# Revit family: Clevertronics_LLIFE-PRO-SM-xx
name_source: partatom
category: Lighting Fixtures
units: mm (PartAtom-declared; Revit-internal decimal feet)

## family parameters
Cut with Voids When Loaded = No
Host = Face
Light Source = Yes
Part Type = Normal
Room Calculation Point = No
Round Connector Dimension = Use Diameter
Shared = No

## types (12) — shared parameters
Apparent Load = 3 VA
Clevertronics_240V LED Strip = 8003081
Clevertronics_AS2293 Classification = C0=D80 C90=D80
Clevertronics_Applicable Standards = AS/NZS3820, CISPR15, AS/NZS2293.3
Clevertronics_Battery = 3.3V 5000mAh
Clevertronics_Battery Type = Lithium Nanophosphate
Clevertronics_Charger Method = Intelligent Current Limited Constant Voltage
Clevertronics_Construction = Polycarbonate Enclosure
Clevertronics_Dimensions Main Enclosure = 242mm x 125mm x 48mm
Clevertronics_Height = 48 mm  [stored 0.15748 ft]
Clevertronics_IP Rating = IP20
Clevertronics_Length = 242 mm  [stored 0.793963 ft]
Clevertronics_Material = Clevertronics_Plycarbonate Base
Clevertronics_Mounting = Surface Mounted
Clevertronics_Operating Mode = Non-maintained
Clevertronics_Operating Temperature = 1˚C to 40˚C
Clevertronics_Operating Voltage = 240V AC; 50Hz
Clevertronics_Replacement Battery = 1530231
Clevertronics_Weight = 0.7Kg
Clevertronics_Width = 125 mm  [stored 0.410105 ft]
Color Filter = 16777215
Default Elevation = 1200 mm
Dimming Lamp Color Temperature Shift = <None>
Lamp = Dual LED (Lifetime warranty on the lamp head and loom assembly)
Manufacturer = Clevertronics
Photometric Web File = LLIFE-PRO-SM_IESA_E_ LL22440_20200331.ies
Tilt Angle = -90.00°
zero-valued in all types: Clevertronics_Annotation Size

## per-type parameters (varying)
| type | Clevertronics_Emergency Driver | Clevertronics_MIC Number | Clevertronics_Power Consumption | Clevertronics_Product Description | Clevertronics_Testing Node | Clevertronics_Testing System | Description | Model |
| LLIFE-PRO-SM_AUT01310080001 | 8003501 | AUT01310080001 | 0.4 Watts (Standby), 2.7 Watts (Max) | Lifelight Pro Emergency, Surface Mount, L10 Nanophosphate, Clevertest Plus |  | Clevertest Plus Enabled (Not activated by default) | Lifelight Pro Emergency, Surface Mount, L10 Nanophosphate, Clevertest Plus | LLIFE-PRO-SM |
| LLIFE-PRO-SM-DALI-BLK_AUT01210580002 | 8003501
8003051 | AUT01210580002 | 0.7 Watts (Standby), 3.0 Watts (Max) | Lifelight Pro Emergency, Surface Mount, L10 Nanophosphate, DALI Emergency, Black | 8003060 | DALI Registered | Lifelight Pro Emergency, Surface Mount, L10 Nanophosphate, DALI Emergency, Black | LLIFE-PRO-SM-DALI-BLK |
| LLIFE-PRO-SM-HV-BLK_AUT02810070001 | 8003501 | AUT02810070001 | 0.7 Watts (Standby), 3.0 Watts (Max) | Lifelight Pro Emergency, Surface Mount, L10 Nanophosphate, Zoneworks XT Hive, Black | 8003191 | Zoneworks XT HIVE (RF) | Lifelight Pro Emergency, Surface Mount, L10 Nanophosphate, Zoneworks XT Hive, Black | LLIFE-PRO-SM-HV-BLK |
| LLIFE-PRO-SM-HV_AUT01810030001 | 8003501
8003501
8003501 | AUT01810030001 | 0.7 Watts (Standby), 3.0 Watts (Max) | Lifelight Pro Emergency, Surface Mount, L10 Nanophosphate, Zoneworks XT Hive | 8003191 | Zoneworks XT HIVE (RF) | Lifelight Pro Emergency, Surface Mount, L10 Nanophosphate, Zoneworks XT Hive | LLIFE-PRO-SM-HV |
| LLIFE-PRO-SM-BLK_AUT01310110001 | 8003501 | AUT01310110001 | 0.4 Watts (Standby), 2.7 Watts (Max) | Lifelight Pro Emergency, Surface Mount, L10 Nanophosphate, Clevertest Plus, Black |  | Clevertest Plus Enabled (Not activated by default) | Lifelight Pro Emergency, Surface Mount, L10 Nanophosphate, Clevertest Plus, Black | LLIFE-PRO-SM-BLK |
| LLIFE-PRO-SM-ZW_AUT01110070001 | 8003501 | AUT01110070001 | 0.7 Watts (Standby), 3.0 Watts (Max) | Lifelight Pro Emergency, Surface Mount, L10 Nanophosphate, Zoneworks | 8001450 | Zoneworks Computerised Testing | Lifelight Pro Emergency, Surface Mount, L10 Nanophosphate, Zoneworks | LLIFE-PRO-SM-ZW |
| LLIFE-PRO-SM-DATA_AUT01410020001 | 8003501 | AUT01410020001 | 0.7 Watts (Standby), 3.0 Watts (Max) | Lifelight Pro Emergency, Surface Mount, L10 Nanophosphate, Zoneworks XT | 8001455 | Zoneworks Computerised Testing | Lifelight Pro Emergency, Surface Mount, L10 Nanophosphate, Zoneworks XT | LLIFE-PRO-SM-DATA |
| LLIFE-PRO-SM-ZW-BLK_AUT01110160001 | 8003501 | AUT01110160001 | 0.7 Watts (Standby), 3.0 Watts (Max) | Lifelight Pro Emergency, Surface Mount, L10 Nanophosphate, Zoneworks XT, Black | 8001450 | Zoneworks Computerised Testing | Lifelight Pro Emergency, Surface Mount, L10 Nanophosphate, Zoneworks XT, Black | LLIFE-PRO-SM-ZW-BLK |
| LLIFE-PRO-SM-D2_AUT01210730001 | 8003501 | AUT01210730001 | 0.7 Watts (Standby), 3.0 Watts (Max) | Lifelight Pro Emergency, Surface Mount, L10 Nanophosphate, DALI-2 | 8003062 | DALI-2 | Lifelight Pro Emergency, Surface Mount, L10 Nanophosphate, DALI-2 | LLIFE-PRO-SM-D2 |
| LLIFE-PRO-SM-HVG-BLK_AUT01910040001 | 8003501 | AUT01910040001 | 0.7 Watts (Standby), 3.0 Watts (Max) | Lifelight Pro Emergency, Surface Mount, L10 Nanophosphate, Zoneworks XT Hive, Black | 8003560 | Zoneworks XT HIVE (RF) 2.4GHz | Lifelight Pro Emergency, Surface Mount, L10 Nanophosphate, Zoneworks XT Hive, Black | LLIFE-PRO-SM-HVG-BLK |
| LLIFE-PRO-SM-HVG_AUT01910020001 | 8003501
8003501
8003501 | AUT01910020001 | 0.7 Watts (Standby), 3.0 Watts (Max) | Lifelight Pro Emergency, Surface Mount, L10 Nanophosphate, Zoneworks XT Hive | 8003560 | Zoneworks XT HIVE (RF) 2.4GHz | Lifelight Pro Emergency, Surface Mount, L10 Nanophosphate, Zoneworks XT Hive | LLIFE-PRO-SM-HVG |
| LLIFE-PRO-SM-DALI_AUT01210570002 | 8003501
8003051 | AUT01210570002 | 0.7 Watts (Standby), 3.0 Watts (Max) | Lifelight Pro Emergency, Surface Mount, L10 Nanophosphate, DALI Emergency | 8003060 | DALI Registered | Lifelight Pro Emergency, Surface Mount, L10 Nanophosphate, DALI Emergency | LLIFE-PRO-SM-DALI |

note: [stored X ft] marks values corroborated as IEEE doubles in the binary element streams (Revit-internal decimal feet)

## geometry (parser evidence)
native form markers: Blend x2, Sweep x3
no freeform markers — native parametric forms only
